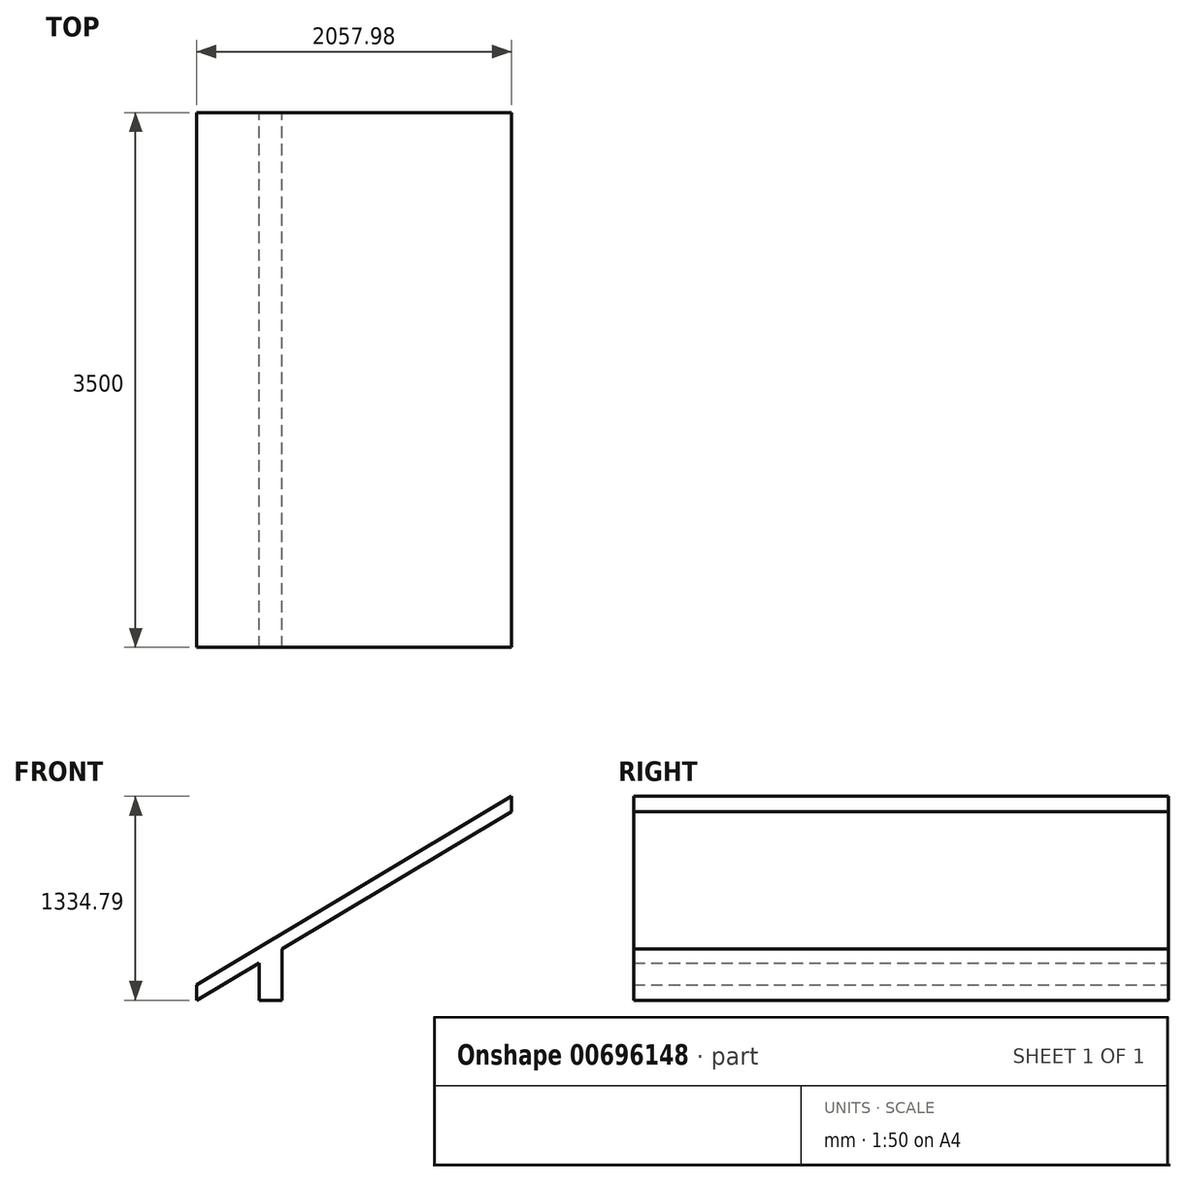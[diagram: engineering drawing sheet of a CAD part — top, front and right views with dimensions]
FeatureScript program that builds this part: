
annotation { "Feature Type Name" : "Feature", "Feature Type Description" : "" }
export const myFeature = defineFeature(function(context is Context, id is Id, definition is map)
    precondition{}
    {
        {
            var Q0;
            Q0=qCreatedBy(makeId("Front.planeOp"),FACE);
            var sketch = newSketch(context, id + "F0", { "sketchPlane" : qUnion([Q0])});
            skLineSegment(sketch, "E0", {"start": v(0, 900) * mm, "end": v(-1500, 0) * mm});
            skLineSegment(sketch, "E1", {"start": v(-1500, 0) * mm, "end": v(-1500, 0) * mm});
            skLineSegment(sketch, "E2", {"start": v(-2057.98, -334.79) * mm, "end": v(-2057.98, -234.79) * mm});
            skLineSegment(sketch, "E3", {"start": v(-2057.98, -234.79) * mm, "end": v(0, 1000) * mm});
            skLineSegment(sketch, "E4", {"start": v(0, 1000) * mm, "end": v(0, 900) * mm});
            skLineSegment(sketch, "E5.bottom", {"start": v(-1500, -334.79) * mm, "end": v(-1650, -334.79) * mm});
            skLineSegment(sketch, "E5.left", {"start": v(-1500, -334.79) * mm, "end": v(-1500, 0) * mm});
            skLineSegment(sketch, "E5.right", {"start": v(-1650, -334.79) * mm, "end": v(-1650, -90) * mm});
            skLineSegment(sketch, "E6.trimOffspring", {"start": v(-1650, -90) * mm, "end": v(-2057.98, -334.79) * mm});
            skSolve(sketch);
        }
        {
            var Q0;
            Q0=qSketchRegion(id+"F0",true);
            extrude(context, id + "F1", {"entities" : qUnion([Q0]), "depth" : 3500 * mm, "offsetDistance" : 25 * mm});
        }
    });
